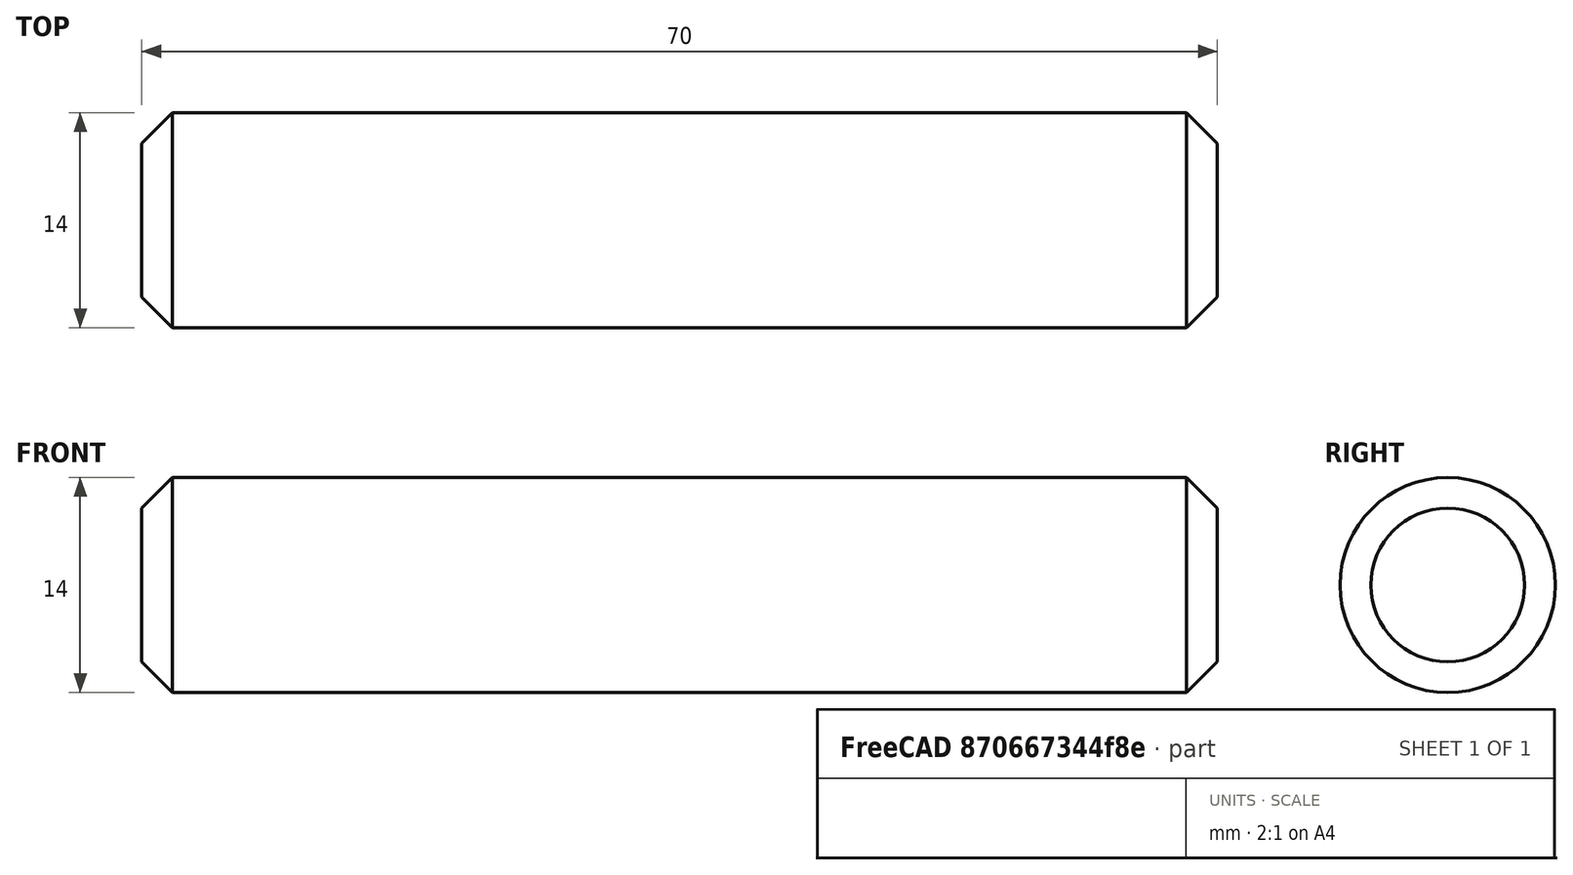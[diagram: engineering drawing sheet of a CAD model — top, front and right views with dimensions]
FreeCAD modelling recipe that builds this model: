
FCSTD DOCUMENT  (FreeCAD 0.21R33771 (Git))
Label: item_04_part_02
License: All rights reserved
LicenseURL: http://en.wikipedia.org/wiki/All_rights_reserved
objects: TechDraw::DrawViewPart×3, TechDraw::DrawViewDimension×2, Sketcher::SketchObject×1, PartDesign::Pad×1, PartDesign::Chamfer×1, PartDesign::Body×1, TechDraw::DrawSVGTemplate×1, TechDraw::DrawViewAnnotation×1, TechDraw::DrawPage×1
note: 9 computed .brp shape members not serialized (recipe doc carries the construction recipe); baked Part::Feature solids carry a one-line shape summary decoded from their .brp

FEATURE [Sketcher::SketchObject] Sketch
  FullyConstrained = true
  MapMode = 5
  Placement = pos=(0,0,0) rot=(0.57735,0.57735,0.57735;2.0944rad)
  Support = -> [YZ_Plane]
  sketch-geometry (1):
    g0: Circle CenterX=0 CenterY=0 CenterZ=0 NormalX=0 NormalY=0 NormalZ=1 AngleXU=0 Radius=7
  constraints (2):
    c: Coincident(g0,g-1)
    c: Diameter(g0) = 14
FEATURE [PartDesign::Pad] Pad
  Direction = (1,-2e-16,3e-16)
  Length = 70
  Length2 = 10
  Placement = pos=(0,0,0) rot=(0.57735,0.57735,0.57735;2.0944rad)
  Profile = -> Sketch
  ReferenceAxis = -> Sketch [N_Axis]
  Type = 0
FEATURE [PartDesign::Chamfer] Chamfer
  Angle = 45
  Base = -> Pad [Edge2,Edge3]
  BaseFeature = -> Pad
  ChamferType = 0
  FlipDirection = false
  Placement = pos=(0,0,0) rot=(0.57735,0.57735,0.57735;2.0944rad)
  Size = 2
  Size2 = 1
  SupportTransform = false
  UseAllEdges = false
FEATURE [PartDesign::Body] Body
  Group = -> [Sketch,Pad,Chamfer]
  Origin = -> Origin
  Tip = -> Chamfer
FEATURE [TechDraw::DrawSVGTemplate] Template
  EditableTexts = Designed_by_Name=Reza Heshmati; Drawing_number=Drawing number; FC-Date=Date; FC-SC=Scale; FC-SH=Sheet; FC-Title=Item #4 (part 2); Subtitle=Subtitle; Weight=Weight
  Height = 210
  Orientation = 1
  Template = <path>
  Width = 297
FEATURE [TechDraw::DrawViewPart] View
  Caption = Side View
  CoarseView = false
  Direction = (0,-1,0)
  Focus = 100
  HardHidden = false
  IsoCount = 0
  IsoHidden = false
  IsoVisible = false
  LockPosition = false
  Perspective = false
  Rotation = 0
  ScaleType = 0
  ScrubCount = 0
  SeamHidden = false
  SeamVisible = false
  SmoothHidden = false
  SmoothVisible = true
  Source = -> [Chamfer]
  X = 178.938
  XDirection = (1,0,0)
  Y = 113.43
FEATURE [TechDraw::DrawViewPart] View001
  Caption = 3D View
  CoarseView = false
  Direction = (0.57735,-0.57735,0.57735)
  Focus = 100
  HardHidden = false
  IsoCount = 0
  IsoHidden = false
  IsoVisible = false
  LockPosition = false
  Perspective = false
  Rotation = 0
  ScaleType = 0
  ScrubCount = 0
  SeamHidden = false
  SeamVisible = false
  SmoothHidden = false
  SmoothVisible = true
  Source = -> [Chamfer]
  X = 73.6391
  XDirection = (0.707107,0.707107,0)
  Y = 152.041
FEATURE [TechDraw::DrawViewPart] View002
  Caption = Front View
  CoarseView = false
  Direction = (1,0,0)
  Focus = 100
  HardHidden = false
  IsoCount = 0
  IsoHidden = false
  IsoVisible = false
  LockPosition = false
  Perspective = false
  Rotation = 0
  ScaleType = 0
  ScrubCount = 0
  SeamHidden = false
  SeamVisible = false
  SmoothHidden = false
  SmoothVisible = true
  Source = -> [Chamfer]
  X = 248.54
  XDirection = (0,1,0)
  Y = 117.506
FEATURE [TechDraw::DrawViewDimension] Dimension
  AngleOverride = false
  Arbitrary = false
  ArbitraryTolerances = false
  EqualTolerance = true
  ExtensionAngle = 0
  FormatSpec = %.2w
  FormatSpecOverTolerance = %+.2w
  FormatSpecUnderTolerance = %+.2w
  Inverted = false
  LineAngle = 0
  LockPosition = false
  MeasureType = 1
  OverTolerance = 0
  References2D = -> [View]
  Rotation = 0
  ScaleType = 0
  TheoreticalExact = false
  Type = 1
  UnderTolerance = 0
  X = -0.423493
  Y = 20.0636
FEATURE [TechDraw::DrawViewDimension] Dimension001
  AngleOverride = false
  Arbitrary = false
  ArbitraryTolerances = false
  EqualTolerance = true
  ExtensionAngle = 0
  FormatSpec = ⌀%.2w
  FormatSpecOverTolerance = %+.2w
  FormatSpecUnderTolerance = %+.2w
  Inverted = false
  LineAngle = 0
  LockPosition = false
  MeasureType = 1
  OverTolerance = 0
  References2D = -> [View002]
  Rotation = 0
  ScaleType = 0
  TheoreticalExact = false
  Type = 5
  UnderTolerance = 0
  X = 18.0054
  Y = 11.5996
FEATURE [TechDraw::DrawViewAnnotation] Annotation
  Caption = Extra Information
  Font = osifont
  LineSpace = 100
  LockPosition = false
  MaxWidth = -1
  Rotation = 0
  ScaleType = 0
  Text = Chamfer = 2
  TextSize = 5
  TextStyle = 0
  X = 48.7012
  Y = 62.0719
FEATURE [TechDraw::DrawPage] Page
  KeepUpdated = true
  NextBalloonIndex = 1
  ProjectionType = 0
  Template = -> Template
  Views = -> [View,View001,View002,Dimension,Dimension001,Annotation]
note: 1 file-system path scrubbed to <path> (originals preserved in the JSON sidecar)
